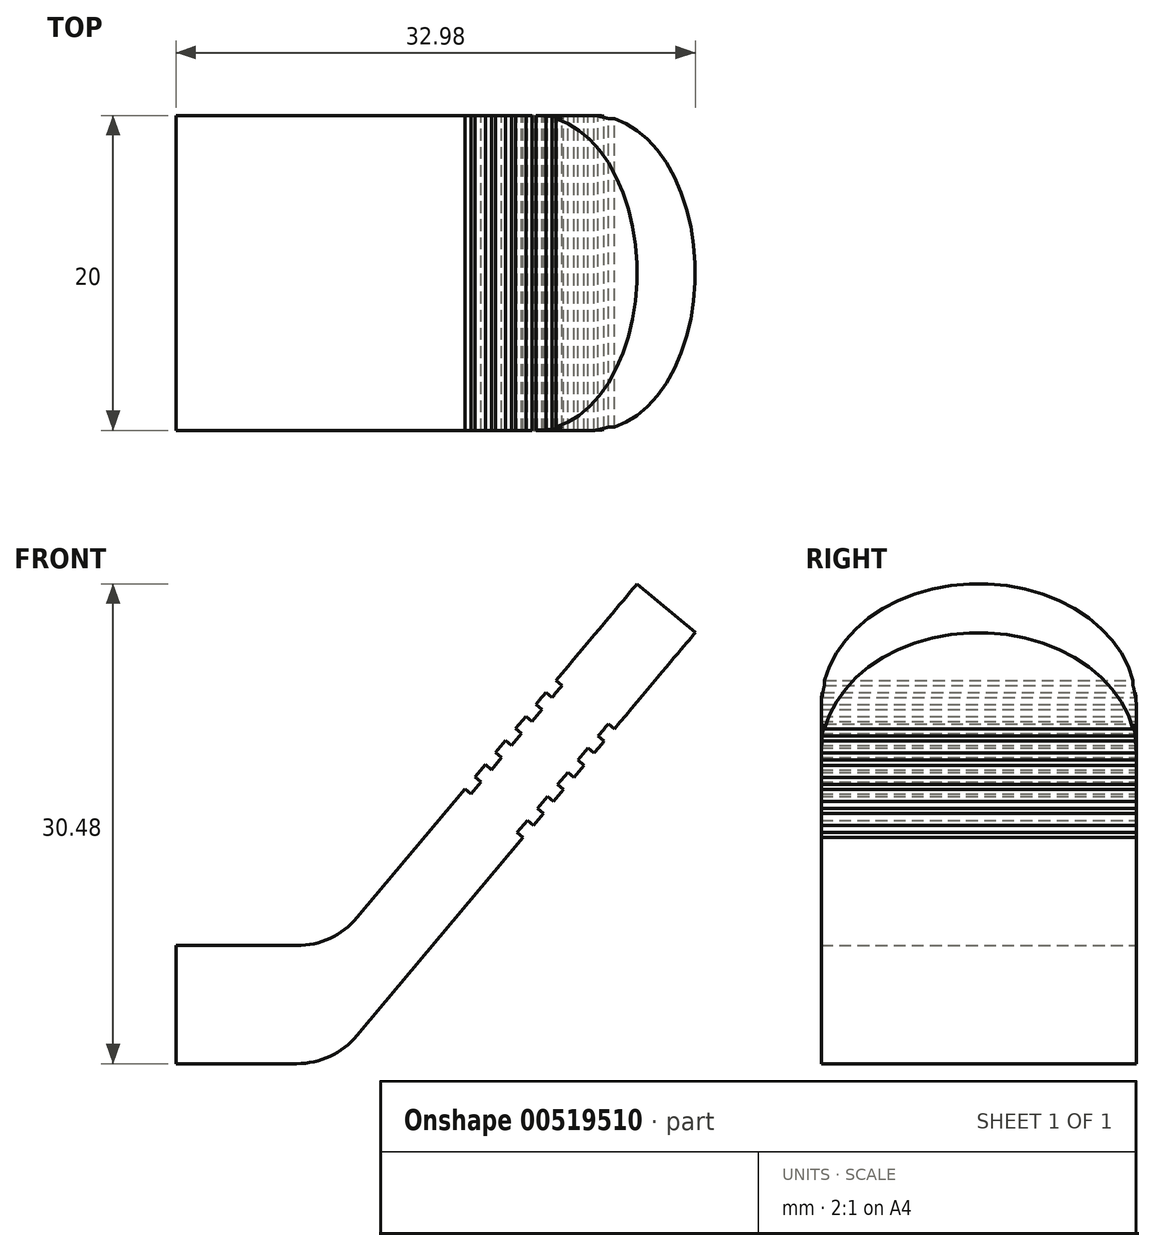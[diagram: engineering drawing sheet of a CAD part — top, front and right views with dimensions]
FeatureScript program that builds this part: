
annotation { "Feature Type Name" : "Feature", "Feature Type Description" : "" }
export const myFeature = defineFeature(function(context is Context, id is Id, definition is map)
    precondition{}
    {
        {
            var Q0;
            Q0=qCreatedBy(makeId("Front.planeOp"),FACE);
            var sketch = newSketch(context, id + "F0", { "sketchPlane" : qUnion([Q0])});
            skLineSegment(sketch, "E0.bottom", {"start": v(0, 0) * mm, "end": v(10, 0) * mm});
            skLineSegment(sketch, "E0.top", {"start": v(0, 7.5) * mm, "end": v(10, 7.5) * mm});
            skLineSegment(sketch, "E0.left", {"start": v(0, 0) * mm, "end": v(0, 7.5) * mm});
            skLineSegment(sketch, "E0.right", {"start": v(10, 0) * mm, "end": v(10, 7.5) * mm});
            skLineSegment(sketch, "E1", {"start": v(10, 7.5) * mm, "end": v(29.28, 30.48) * mm});
            skLineSegment(sketch, "E2", {"start": v(10, 7.5) * mm, "end": v(10, 38.33) * mm, "construction": true});
            skLineSegment(sketch, "E3", {"start": v(29.28, 30.48) * mm, "end": v(39, 22.32) * mm, "construction": true});
            skLineSegment(sketch, "E4", {"start": v(10, 0) * mm, "end": v(32.98, 27.38) * mm});
            skLineSegment(sketch, "E5", {"start": v(29.28, 30.48) * mm, "end": v(32.98, 27.38) * mm});
            skLineSegment(sketch, "E6", {"start": v(10, 3.75) * mm, "end": v(31.13, 28.93) * mm, "construction": true});
            skLineSegment(sketch, "E7", {"start": v(24.14, 24.35) * mm, "end": v(24.52, 24.03) * mm});
            skLineSegment(sketch, "E8", {"start": v(24.52, 24.03) * mm, "end": v(23.88, 23.27) * mm});
            skLineSegment(sketch, "E9", {"start": v(23.88, 23.27) * mm, "end": v(23.5, 23.59) * mm});
            skLineSegment(sketch, "E10.1.0.0", {"start": v(22.6, 21.73) * mm, "end": v(22.21, 22.05) * mm});
            skLineSegment(sketch, "E10.1.0.1", {"start": v(23.24, 22.5) * mm, "end": v(22.6, 21.73) * mm});
            skLineSegment(sketch, "E10.1.0.2", {"start": v(22.86, 22.82) * mm, "end": v(23.24, 22.5) * mm});
            skLineSegment(sketch, "E10.2.0.0", {"start": v(21.31, 20.2) * mm, "end": v(20.93, 20.52) * mm});
            skLineSegment(sketch, "E10.2.0.1", {"start": v(21.95, 20.97) * mm, "end": v(21.31, 20.2) * mm});
            skLineSegment(sketch, "E10.2.0.2", {"start": v(21.57, 21.29) * mm, "end": v(21.95, 20.97) * mm});
            skLineSegment(sketch, "E10.3.0.0", {"start": v(20.02, 18.67) * mm, "end": v(19.64, 19) * mm});
            skLineSegment(sketch, "E10.3.0.1", {"start": v(20.67, 19.44) * mm, "end": v(20.02, 18.67) * mm});
            skLineSegment(sketch, "E10.3.0.2", {"start": v(20.28, 19.76) * mm, "end": v(20.67, 19.44) * mm});
            skLineSegment(sketch, "E10.4.0.0", {"start": v(18.74, 17.14) * mm, "end": v(18.36, 17.46) * mm});
            skLineSegment(sketch, "E10.4.0.1", {"start": v(19.38, 17.9) * mm, "end": v(18.74, 17.14) * mm});
            skLineSegment(sketch, "E10.4.0.2", {"start": v(19, 18.22) * mm, "end": v(19.38, 17.9) * mm});
            skLineSegment(sketch, "E10.direction1", {"start": v(23.88, 23.27) * mm, "end": v(22.6, 21.73) * mm, "construction": true});
            skLineSegment(sketch, "E11.MirrorCS", {"start": v(27.83, 21.25) * mm, "end": v(27.45, 21.58) * mm});
            skLineSegment(sketch, "E12.MirrorCS", {"start": v(27.45, 21.58) * mm, "end": v(26.8, 20.8) * mm});
            skLineSegment(sketch, "E13.MirrorCS", {"start": v(26.8, 20.8) * mm, "end": v(27.2, 20.49) * mm});
            skLineSegment(sketch, "E14.MirrorCS", {"start": v(26.55, 19.72) * mm, "end": v(26.17, 20.04) * mm});
            skLineSegment(sketch, "E15.MirrorCS", {"start": v(25.52, 19.28) * mm, "end": v(25.9, 18.96) * mm});
            skLineSegment(sketch, "E16.MirrorCS", {"start": v(25.26, 18.19) * mm, "end": v(24.88, 18.51) * mm});
            skLineSegment(sketch, "E17.MirrorCS", {"start": v(24.88, 18.51) * mm, "end": v(24.24, 17.75) * mm});
            skLineSegment(sketch, "E18.MirrorCS", {"start": v(24.24, 17.75) * mm, "end": v(24.62, 17.42) * mm});
            skLineSegment(sketch, "E19.MirrorCS", {"start": v(23.98, 16.66) * mm, "end": v(23.6, 16.98) * mm});
            skLineSegment(sketch, "E20.MirrorCS", {"start": v(23.6, 16.98) * mm, "end": v(22.95, 16.21) * mm});
            skLineSegment(sketch, "E21.MirrorCS", {"start": v(22.95, 16.21) * mm, "end": v(23.33, 15.9) * mm});
            skLineSegment(sketch, "E22.MirrorCS", {"start": v(22.7, 15.13) * mm, "end": v(22.3, 15.45) * mm});
            skLineSegment(sketch, "E23.MirrorCS", {"start": v(22.3, 15.45) * mm, "end": v(21.67, 14.68) * mm});
            skLineSegment(sketch, "E24.MirrorCS", {"start": v(21.67, 14.68) * mm, "end": v(22.05, 14.36) * mm});
            skLineSegment(sketch, "E25", {"start": v(25.52, 19.28) * mm, "end": v(26.17, 20.04) * mm});
            skLineSegment(sketch, "E26", {"start": v(23.5, 23.59) * mm, "end": v(24.14, 24.35) * mm});
            skLineSegment(sketch, "E27", {"start": v(22.86, 22.82) * mm, "end": v(22.21, 22.05) * mm});
            skLineSegment(sketch, "E28", {"start": v(21.57, 21.29) * mm, "end": v(20.93, 20.52) * mm});
            skLineSegment(sketch, "E29", {"start": v(20.28, 19.76) * mm, "end": v(19.64, 19) * mm});
            skLineSegment(sketch, "E30", {"start": v(19, 18.22) * mm, "end": v(18.36, 17.46) * mm});
            skLineSegment(sketch, "E31", {"start": v(27.83, 21.25) * mm, "end": v(27.2, 20.49) * mm});
            skLineSegment(sketch, "E32", {"start": v(26.55, 19.72) * mm, "end": v(25.9, 18.96) * mm});
            skLineSegment(sketch, "E33", {"start": v(25.26, 18.19) * mm, "end": v(24.62, 17.42) * mm});
            skLineSegment(sketch, "E34", {"start": v(23.98, 16.66) * mm, "end": v(23.33, 15.9) * mm});
            skLineSegment(sketch, "E35", {"start": v(22.7, 15.13) * mm, "end": v(22.05, 14.36) * mm});
            skSolve(sketch);
        }
        {
            var Q0;
            Q0=makeQuery(id+"F0.imprint","IMPRINT",FACE,{"disambiguationData":[TD([[makeQuery(id+"F0.imprint","IMPRINT",EDGE,{"derivedFrom":sQuery(id+"F0.wireOp",EDGE,"E0.bottom")}),1.0]])]});
            var Q1;
            {var subQ22=sQuery(id+"F0.wireOp",EDGE,"E0.right");Q1=makeQuery(id+"F0.imprint","IMPRINT",FACE,{"disambiguationData":[TD([[makeQuery(id+"F0.imprint","IMPRINT",EDGE,{"derivedFrom":subQ22}),-1.0]])]});}
            extrude(context, id + "F1", {"entities" : qUnion([Q0, Q1]), "depth" : 20 * mm, "offsetDistance" : 25 * mm});
        }
        {
            var Q0;
            Q0=makeQuery(id+"F1.opExtrude","SWEPT_EDGE",EDGE,{"disambiguationData":[OSD([sQuery(id+"F0.wireOp",EDGE,"E0.top"),sQuery(id+"F0.wireOp",EDGE,"E0.right"),sQuery(id+"F0.wireOp",EDGE,"E1")])]});
            fillet(context, id + "F2", {"entities" : qUnion([Q0]), "radius" : 5 * mm, "tangentPropagation" : true, "allowEdgeOverflow" : false});
        }
        {
            var Q0;
            Q0=makeQuery(id+"F1.opExtrude","CAP_EDGE",EDGE,{"disambiguationData":[OSD([sQuery(id+"F0.wireOp",EDGE,"E5")])],"isStart":false});
            var Q1;
            Q1=makeQuery(id+"F1.opExtrude","CAP_EDGE",EDGE,{"disambiguationData":[OSD([sQuery(id+"F0.wireOp",EDGE,"E5")])],"isStart":true});
            fillet(context, id + "F3", {"entities" : qUnion([Q0, Q1]), "radius" : 10 * mm, "tangentPropagation" : true, "allowEdgeOverflow" : false});
        }
        {
            var Q0;
            Q0=makeQuery(id+"F1.opExtrude","SWEPT_EDGE",EDGE,{"disambiguationData":[OSD([sQuery(id+"F0.wireOp",EDGE,"E0.bottom"),sQuery(id+"F0.wireOp",EDGE,"E0.right"),sQuery(id+"F0.wireOp",EDGE,"E4")])]});
            fillet(context, id + "F4", {"entities" : qUnion([Q0]), "radius" : 5 * mm, "tangentPropagation" : true, "allowEdgeOverflow" : false});
        }
    });
